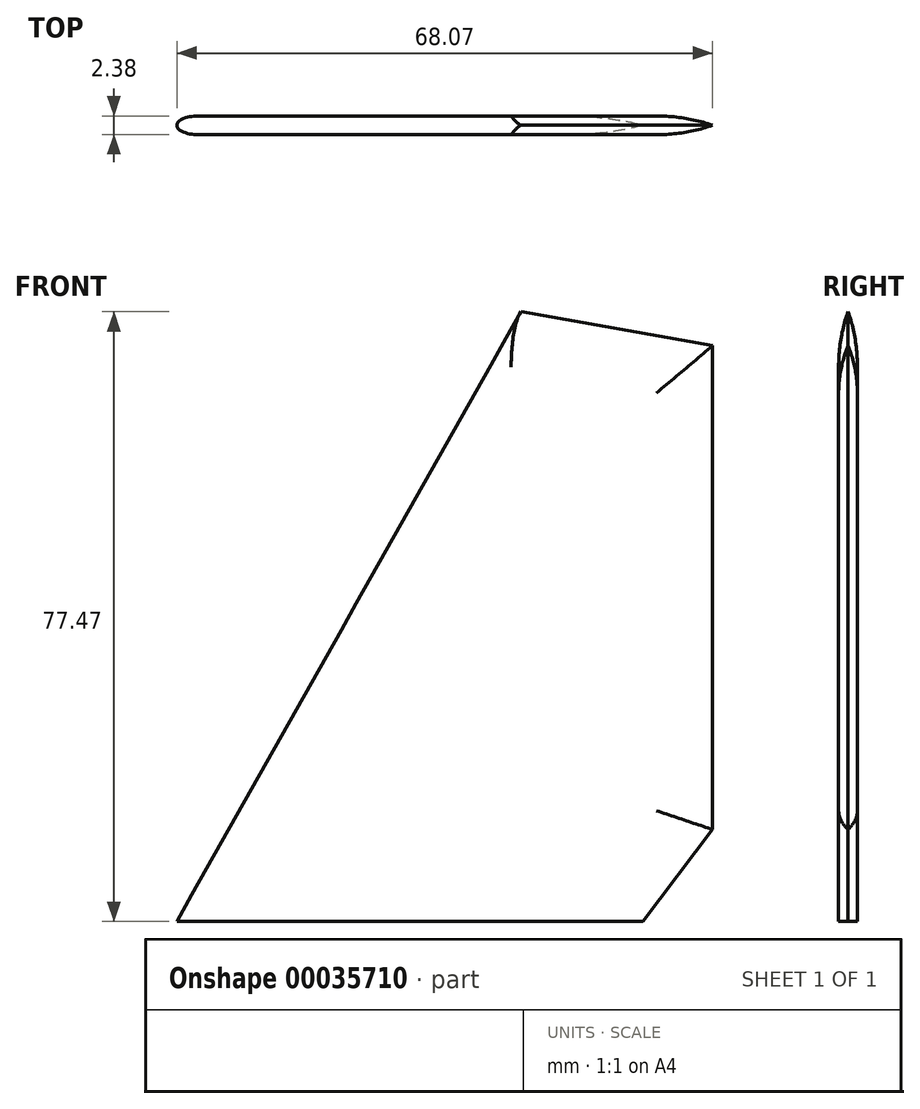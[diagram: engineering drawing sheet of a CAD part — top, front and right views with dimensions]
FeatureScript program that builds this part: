
annotation { "Feature Type Name" : "Feature", "Feature Type Description" : "" }
export const myFeature = defineFeature(function(context is Context, id is Id, definition is map)
    precondition{}
    {
        {
            var Q0;
            Q0=qCreatedBy(makeId("Front.planeOp"),FACE);
            var sketch = newSketch(context, id + "F0", { "sketchPlane" : qUnion([Q0])});
            skLineSegment(sketch, "E0", {"start": v(59.18, 0) * mm, "end": v(0, 0) * mm});
            skLineSegment(sketch, "E1", {"start": v(61.47, 64.82) * mm, "end": v(61.47, 11.68) * mm});
            skLineSegment(sketch, "E2", {"start": v(56.13, 57.67) * mm, "end": v(56.13, 11.68) * mm});
            skLineSegment(sketch, "E3", {"start": v(68.07, 73.15) * mm, "end": v(68.07, 11.68) * mm});
            skLineSegment(sketch, "E4", {"start": v(0, 0) * mm, "end": v(43.69, 77.47) * mm});
            skLineSegment(sketch, "E5", {"start": v(68.07, 11.68) * mm, "end": v(6.59, 11.68) * mm, "construction": true});
            skLineSegment(sketch, "E6", {"start": v(34.66, 61.47) * mm, "end": v(56.13, 57.67) * mm});
            skLineSegment(sketch, "E7", {"start": v(38.82, 68.83) * mm, "end": v(61.47, 64.82) * mm});
            skLineSegment(sketch, "E8", {"start": v(43.69, 77.47) * mm, "end": v(68.07, 73.15) * mm});
            skLineSegment(sketch, "E9", {"start": v(56.13, 11.68) * mm, "end": v(47.24, 0) * mm});
            skLineSegment(sketch, "E10", {"start": v(61.47, 11.68) * mm, "end": v(52.58, 0) * mm});
            skLineSegment(sketch, "E11", {"start": v(68.07, 11.68) * mm, "end": v(59.18, 0) * mm});
            skSolve(sketch);
        }
        {
            var Q0;
            Q0=makeQuery(id+"F0.imprint","IMPRINT",FACE,{"disambiguationData":[TD([[makeQuery(id+"F0.imprint","IMPRINT",EDGE,{"derivedFrom":sQuery(id+"F0.wireOp",EDGE,"E2")}),-1.0]])]});
            var Q1;
            Q1=makeQuery(id+"F0.imprint","IMPRINT",FACE,{"disambiguationData":[TD([[makeQuery(id+"F0.imprint","IMPRINT",EDGE,{"derivedFrom":sQuery(id+"F0.wireOp",EDGE,"E1")}),-1.0]])]});
            var Q2;
            Q2=makeQuery(id+"F0.imprint","IMPRINT",FACE,{"disambiguationData":[TD([[makeQuery(id+"F0.imprint","IMPRINT",EDGE,{"derivedFrom":sQuery(id+"F0.wireOp",EDGE,"E1")}),1.0]])]});
            extrude(context, id + "F1", {"entities" : qUnion([Q0, Q1, Q2]), "depth" : 2.38 * mm, "symmetric" : true});
        }
        {
            var Q0;
            Q0=sQuery(id+"F0.wireOp",EDGE,"E4");
            var Q1;
            Q1=sQuery(id+"F0.wireOp",VERTEX,"E4.start");
            cPlane(context, id + "F2", {"entities" : qUnion([Q0, Q1]), "cplaneType" : CPlaneType.LINE_POINT, "offset" : 152.4 * mm, "width" : 152.4 * mm, "height" : 152.4 * mm});
        }
        {
            var Q0;
            Q0=qCreatedBy(id+"F2.planeOp",FACE);
            var sketch = newSketch(context, id + "F3", { "sketchPlane" : qUnion([Q0])});
            skLineSegment(sketch, "E12.0", {"start": v(0, 1.2) * mm, "end": v(23.36, 1.2) * mm, "construction": true});
            skLineSegment(sketch, "E12.1", {"start": v(0, -1.2) * mm, "end": v(23.36, -1.2) * mm, "construction": true});
            skLineSegment(sketch, "E12.2", {"start": v(0, -1.2) * mm, "end": v(0, 1.2) * mm, "construction": true});
            skLineSegment(sketch, "E13", {"start": v(2.38, -1.2) * mm, "end": v(2.38, 1.2) * mm, "construction": true});
            skLineSegment(sketch, "E14", {"start": v(2.38, 1.2) * mm, "end": v(2.38, 3.73) * mm});
            skLineSegment(sketch, "E15", {"start": v(2.38, 3.73) * mm, "end": v(-2.54, 3.73) * mm});
            skLineSegment(sketch, "E16", {"start": v(-2.54, 3.73) * mm, "end": v(-2.54, 0) * mm});
            skLineSegment(sketch, "E17", {"start": v(0, 0) * mm, "end": v(2.38, 0) * mm, "construction": true});
            skLineSegment(sketch, "E18", {"start": v(2.38, 0) * mm, "end": v(0, 0) * mm, "construction": true});
            skEllipticalArc(sketch, "E19", {});
            skLineSegment(sketch, "E20.MirrorCS", {"start": v(-2.54, -3.73) * mm, "end": v(-2.54, 0) * mm});
            skLineSegment(sketch, "E21.MirrorCS", {"start": v(2.38, -3.73) * mm, "end": v(-2.54, -3.73) * mm});
            skLineSegment(sketch, "E22.MirrorCS", {"start": v(2.38, -1.2) * mm, "end": v(2.38, -3.73) * mm});
            const initialGuessF3  = {"E19": [0.00238125, 0, -1, 0, 0.0023812499999999997, 0.001190625, 4.71238898038469, 1.5707963267948966]};
            skSetInitialGuess(sketch, initialGuessF3);
            skSolve(sketch);
        }
        {
            var Q0;
            Q0=makeQuery(id+"F3.imprint","IMPRINT",FACE,{"disambiguationData":[TD([[makeQuery(id+"F3.imprint","IMPRINT",EDGE,{"derivedFrom":sQuery(id+"F3.wireOp",EDGE,"E14")}),1.0]])]});
            extrude(context, id + "F4", {"entities" : qUnion([Q0]), "operationType" : NewBodyOperationType.REMOVE, "endBound" : BoundingType.THROUGH_ALL, "depth" : 25.4 * mm});
        }
        {
            var Q0;
            Q0=sQuery(id+"F0.wireOp",EDGE,"E11");
            var Q1;
            Q1=sQuery(id+"F0.wireOp",VERTEX,"E11.end");
            cPlane(context, id + "F5", {"entities" : qUnion([Q0, Q1]), "cplaneType" : CPlaneType.LINE_POINT, "offset" : 152.4 * mm, "width" : 152.4 * mm, "height" : 152.4 * mm});
        }
        {
            var Q0;
            Q0=qCreatedBy(id+"F5.planeOp",FACE);
            var sketch = newSketch(context, id + "F6", { "sketchPlane" : qUnion([Q0])});
            skLineSegment(sketch, "E23.0", {"start": v(9.88, -1.2) * mm, "end": v(47.1, -1.2) * mm, "construction": true});
            skLineSegment(sketch, "E23.1", {"start": v(47.1, 1.2) * mm, "end": v(47.1, -1.2) * mm, "construction": true});
            skLineSegment(sketch, "E23.2", {"start": v(9.88, 1.2) * mm, "end": v(47.1, 1.2) * mm, "construction": true});
            skLineSegment(sketch, "E24", {"start": v(39.95, 1.2) * mm, "end": v(39.95, -1.2) * mm, "construction": true});
            skLineSegment(sketch, "E25", {"start": v(39.95, -1.2) * mm, "end": v(39.95, -3.73) * mm});
            skLineSegment(sketch, "E26", {"start": v(39.95, -3.73) * mm, "end": v(49.64, -3.73) * mm});
            skLineSegment(sketch, "E27", {"start": v(49.64, -3.73) * mm, "end": v(49.64, 0) * mm});
            skArc(sketch, "E28", {"start": v(39.95, -1.2) * mm, "mid": v(43.58, -0.9) * mm, "end": v(47.1, 0) * mm});
            skPoint(sketch, "E28.startSnap0", {"position": v(47.1, 0) * mm});
            skPoint(sketch, "E29.orphan", {"position": v(32.81, 0) * mm});
            skArc(sketch, "E30.MirrorCS", {"start": v(39.95, 1.2) * mm, "mid": v(43.58, 0.9) * mm, "end": v(47.1, 0) * mm});
            skLineSegment(sketch, "E31.MirrorCS", {"start": v(39.95, 1.2) * mm, "end": v(39.95, 3.73) * mm});
            skLineSegment(sketch, "E32.MirrorCS", {"start": v(39.95, 3.73) * mm, "end": v(49.64, 3.73) * mm});
            skLineSegment(sketch, "E33.MirrorCS", {"start": v(49.64, 3.73) * mm, "end": v(49.64, 0) * mm});
            skSolve(sketch);
        }
        {
            var Q0;
            Q0=makeQuery(id+"F6.imprint","IMPRINT",FACE,{"disambiguationData":[TD([[makeQuery(id+"F6.imprint","IMPRINT",EDGE,{"derivedFrom":sQuery(id+"F6.wireOp",EDGE,"E25")}),1.0]])]});
            extrude(context, id + "F7", {"entities" : qUnion([Q0]), "operationType" : NewBodyOperationType.REMOVE, "oppositeDirection" : true, "depth" : 76.2 * mm, "symmetric" : true});
        }
        {
            var Q0;
            Q0=qCreatedBy(makeId("Top.planeOp"),FACE);
            var sketch = newSketch(context, id + "F8", { "sketchPlane" : qUnion([Q0])});
            skLineSegment(sketch, "E34.0", {"start": v(46.17, -1.2) * mm, "end": v(68.07, -1.2) * mm, "construction": true});
            skLineSegment(sketch, "E34.1", {"start": v(46.17, 1.2) * mm, "end": v(68.07, 1.2) * mm, "construction": true});
            skLineSegment(sketch, "E34.2", {"start": v(68.07, -1.2) * mm, "end": v(68.07, 1.2) * mm, "construction": true});
            skLineSegment(sketch, "E35", {"start": v(60.93, -1.2) * mm, "end": v(60.93, 1.2) * mm, "construction": true});
            skLineSegment(sketch, "E36", {"start": v(60.93, 1.2) * mm, "end": v(60.93, 3.73) * mm});
            skLineSegment(sketch, "E37", {"start": v(60.93, 3.73) * mm, "end": v(70.61, 3.73) * mm});
            skLineSegment(sketch, "E38", {"start": v(70.61, 3.73) * mm, "end": v(70.61, 0) * mm});
            skArc(sketch, "E39", {"start": v(68.07, 0) * mm, "mid": v(64.55, 0.9) * mm, "end": v(60.93, 1.2) * mm});
            skPoint(sketch, "E39.endSnap0", {"position": v(68.07, 0) * mm});
            skPoint(sketch, "E40.orphan", {"position": v(53.78, 0) * mm});
            skArc(sketch, "E41.MirrorCS", {"start": v(68.07, 0) * mm, "mid": v(64.55, -0.9) * mm, "end": v(60.93, -1.2) * mm});
            skLineSegment(sketch, "E42.MirrorCS", {"start": v(60.93, -1.2) * mm, "end": v(60.93, -3.73) * mm});
            skLineSegment(sketch, "E43.MirrorCS", {"start": v(60.93, -3.73) * mm, "end": v(70.61, -3.73) * mm});
            skLineSegment(sketch, "E44.MirrorCS", {"start": v(70.61, -3.73) * mm, "end": v(70.61, 0) * mm});
            skSolve(sketch);
        }
        {
            var Q0;
            Q0=makeQuery(id+"F8.imprint","IMPRINT",FACE,{"disambiguationData":[TD([[makeQuery(id+"F8.imprint","IMPRINT",EDGE,{"derivedFrom":sQuery(id+"F8.wireOp",EDGE,"E36")}),-1.0]])]});
            extrude(context, id + "F9", {"entities" : qUnion([Q0]), "operationType" : NewBodyOperationType.REMOVE, "endBound" : BoundingType.THROUGH_ALL, "depth" : 25.4 * mm});
        }
        {
            var Q0;
            Q0=sQuery(id+"F0.wireOp",EDGE,"E8");
            var Q1;
            Q1=sQuery(id+"F0.wireOp",VERTEX,"E3.start");
            cPlane(context, id + "F10", {"entities" : qUnion([Q0, Q1]), "cplaneType" : CPlaneType.LINE_POINT, "offset" : 152.4 * mm, "width" : 152.4 * mm, "height" : 152.4 * mm});
        }
        {
            var Q0;
            Q0=qCreatedBy(id+"F10.planeOp",FACE);
            var sketch = newSketch(context, id + "F11", { "sketchPlane" : qUnion([Q0])});
            skLineSegment(sketch, "E45.0", {"start": v(-1.2, 83.9) * mm, "end": v(-1.2, 0.48) * mm, "construction": true});
            skFitSpline(sketch, "E45.1", {"points": [v(-1.2, 83.9) * mm, v(-0.4, 83.9) * mm, v(0.4, 83.9) * mm, v(1.2, 83.9) * mm], "construction": true});
            skLineSegment(sketch, "E45.2", {"start": v(1.2, 83.9) * mm, "end": v(1.2, 0.48) * mm, "construction": true});
            skLineSegment(sketch, "E46", {"start": v(-1.2, 76.76) * mm, "end": v(1.2, 76.76) * mm, "construction": true});
            skLineSegment(sketch, "E47", {"start": v(1.2, 76.76) * mm, "end": v(3.73, 76.76) * mm});
            skLineSegment(sketch, "E48", {"start": v(3.73, 76.76) * mm, "end": v(3.73, 86.44) * mm});
            skLineSegment(sketch, "E49", {"start": v(3.73, 86.44) * mm, "end": v(0, 86.44) * mm});
            skArc(sketch, "E50", {"start": v(1.2, 76.76) * mm, "mid": v(0.9, 80.38) * mm, "end": v(0, 83.9) * mm});
            skPoint(sketch, "E51.orphan", {"position": v(0, 69.61) * mm});
            skArc(sketch, "E52.MirrorCS", {"start": v(-1.2, 76.76) * mm, "mid": v(-0.9, 80.38) * mm, "end": v(0, 83.9) * mm});
            skLineSegment(sketch, "E53.MirrorCS", {"start": v(-1.2, 76.76) * mm, "end": v(-3.73, 76.76) * mm});
            skLineSegment(sketch, "E54.MirrorCS", {"start": v(-3.73, 76.76) * mm, "end": v(-3.73, 86.44) * mm});
            skLineSegment(sketch, "E55.MirrorCS", {"start": v(-3.73, 86.44) * mm, "end": v(0, 86.44) * mm});
            skSolve(sketch);
        }
        {
            var Q0;
            Q0=makeQuery(id+"F11.imprint","IMPRINT",FACE,{"disambiguationData":[TD([[makeQuery(id+"F11.imprint","IMPRINT",EDGE,{"derivedFrom":sQuery(id+"F11.wireOp",EDGE,"E47")}),1.0]])]});
            extrude(context, id + "F12", {"entities" : qUnion([Q0]), "operationType" : NewBodyOperationType.REMOVE, "oppositeDirection" : true, "depth" : 76.2 * mm, "symmetric" : true});
        }
    });
